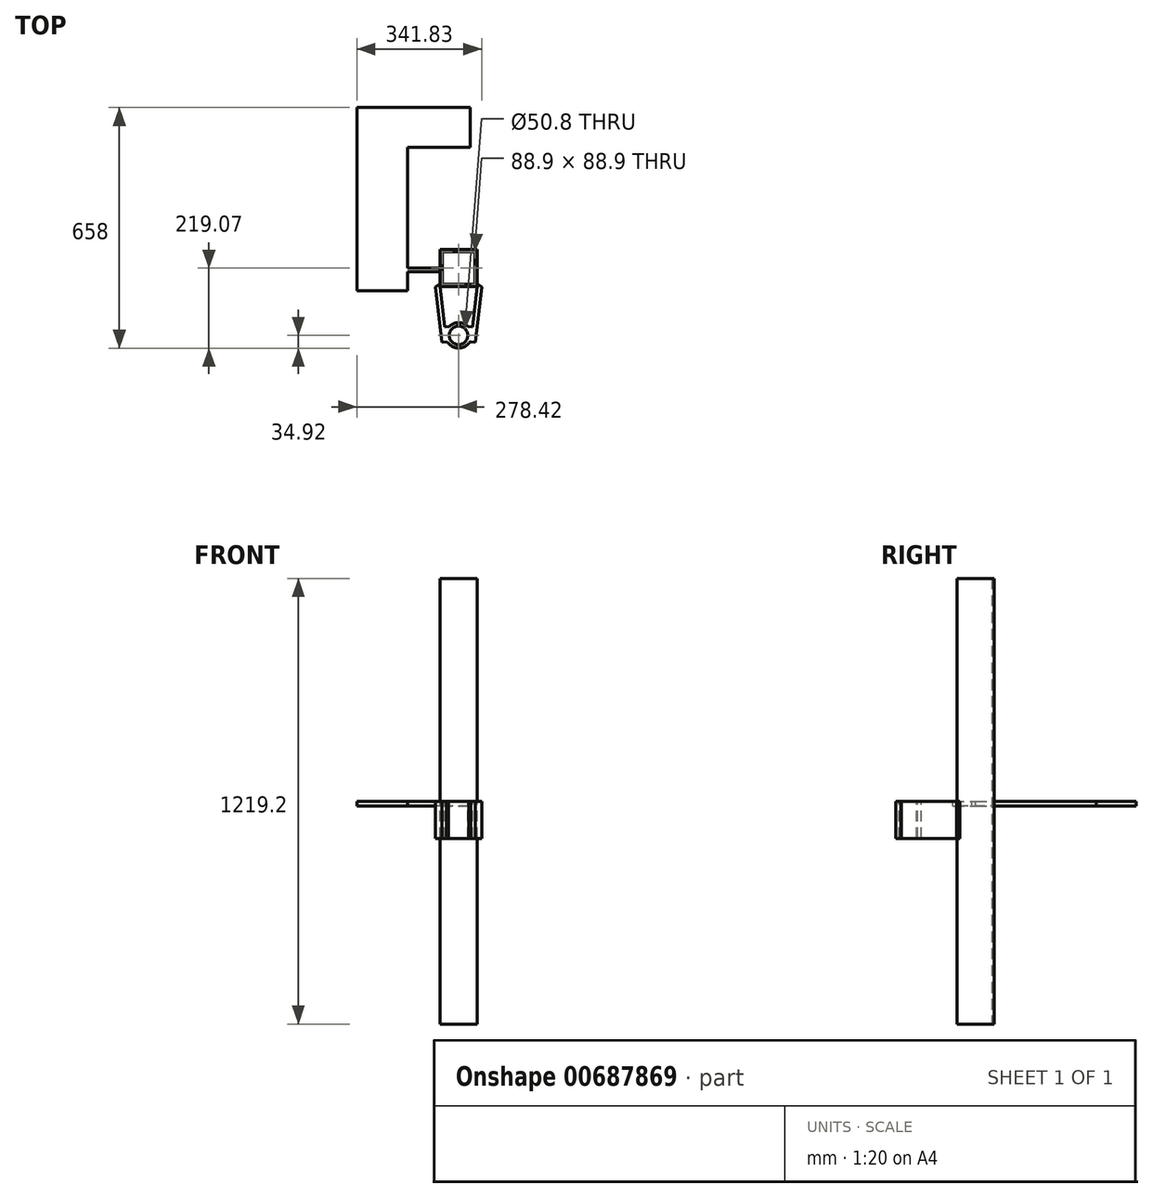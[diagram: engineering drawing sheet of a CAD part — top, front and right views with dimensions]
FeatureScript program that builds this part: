
annotation { "Feature Type Name" : "Feature", "Feature Type Description" : "" }
export const myFeature = defineFeature(function(context is Context, id is Id, definition is map)
    precondition{}
    {
        {
            var Q0;
            Q0=qCreatedBy(makeId("Top.planeOp"),FACE);
            var sketch = newSketch(context, id + "F0", { "sketchPlane" : qUnion([Q0])});
            skLineSegment(sketch, "E0.bottom", {"start": v(-50.8, -50.8) * mm, "end": v(50.8, -50.8) * mm});
            skLineSegment(sketch, "E0.top", {"start": v(-50.8, 50.8) * mm, "end": v(50.8, 50.8) * mm});
            skLineSegment(sketch, "E0.left", {"start": v(-50.8, -50.8) * mm, "end": v(-50.8, 50.8) * mm});
            skLineSegment(sketch, "E0.right", {"start": v(50.8, -50.8) * mm, "end": v(50.8, 50.8) * mm});
            skLineSegment(sketch, "E1.bottom", {"start": v(-44.45, 44.45) * mm, "end": v(44.45, 44.45) * mm});
            skLineSegment(sketch, "E1.top", {"start": v(-44.45, -44.45) * mm, "end": v(44.45, -44.45) * mm});
            skLineSegment(sketch, "E1.left", {"start": v(-44.45, 44.45) * mm, "end": v(-44.45, -44.45) * mm});
            skLineSegment(sketch, "E1.right", {"start": v(44.45, 44.45) * mm, "end": v(44.45, -44.45) * mm});
            skSolve(sketch);
        }
        {
            var Q0;
            Q0=makeQuery(id+"F0.imprint","IMPRINT",FACE,{"disambiguationData":[TD([[makeQuery(id+"F0.imprint","IMPRINT",EDGE,{"derivedFrom":sQuery(id+"F0.wireOp",EDGE,"E0.bottom")}),1.0]])]});
            extrude(context, id + "F1", {"entities" : qUnion([Q0]), "depth" : 1219.2 * mm, "offsetDistance" : 25.4 * mm});
        }
        {
            var Q0;
            Q0=qCreatedBy(makeId("Top.planeOp"),FACE);
            cPlane(context, id + "F2", {"entities" : qUnion([Q0]), "cplaneType" : CPlaneType.OFFSET, "offset" : 609.6 * mm, "width" : 152.4 * mm, "height" : 152.4 * mm});
        }
        {
            var Q0;
            Q0=qCreatedBy(id+"F2.planeOp",FACE);
            var sketch = newSketch(context, id + "F3", { "sketchPlane" : qUnion([Q0])});
            skLineSegment(sketch, "E2.0", {"start": v(-50.8, -50.8) * mm, "end": v(-50.8, 50.8) * mm});
            skLineSegment(sketch, "E3.0", {"start": v(-50.8, 50.8) * mm, "end": v(50.8, 50.8) * mm});
            skLineSegment(sketch, "E4.0", {"start": v(50.8, -50.8) * mm, "end": v(50.8, 50.8) * mm});
            skLineSegment(sketch, "E5.0", {"start": v(-50.8, -50.8) * mm, "end": v(50.8, -50.8) * mm});
            skCircle(sketch, "E6", {"center": v(0, -184.15) * mm, "radius": 34.93 * mm});
            skCircle(sketch, "E7", {"center": v(0, -184.15) * mm, "radius": 25.4 * mm});
            skLineSegment(sketch, "E8", {"start": v(-50.8, -50.8) * mm, "end": v(-33.05, -202.16) * mm});
            skLineSegment(sketch, "E9", {"start": v(50.8, -50.8) * mm, "end": v(33.05, -202.16) * mm});
            skLineSegment(sketch, "E10.0", {"start": v(-63.41, -52.28) * mm, "end": v(-45.67, -203.64) * mm});
            skLineSegment(sketch, "E11.0", {"start": v(63.41, -52.28) * mm, "end": v(45.67, -203.64) * mm});
            skLineSegment(sketch, "E12", {"start": v(-50.8, -50.8) * mm, "end": v(-63.41, -52.28) * mm});
            skLineSegment(sketch, "E13", {"start": v(63.41, -52.28) * mm, "end": v(50.8, -50.8) * mm});
            skLineSegment(sketch, "E14", {"start": v(45.67, -203.64) * mm, "end": v(33.05, -202.16) * mm});
            skLineSegment(sketch, "E15", {"start": v(-33.05, -202.16) * mm, "end": v(-45.67, -203.64) * mm});
            skLineSegment(sketch, "E16", {"start": v(-37.83, -161.4) * mm, "end": v(-25.16, -159.92) * mm});
            skLineSegment(sketch, "E17", {"start": v(37.83, -161.4) * mm, "end": v(25.16, -159.92) * mm});
            skLineSegment(sketch, "E18", {"start": v(33.05, -202.16) * mm, "end": v(28.17, -204.79) * mm});
            skLineSegment(sketch, "E19", {"start": v(-33.05, -202.16) * mm, "end": v(-27.98, -205.05) * mm});
            skLineSegment(sketch, "E20", {"start": v(-63.41, -52.28) * mm, "end": v(-50.8, -42.6) * mm});
            skLineSegment(sketch, "E21", {"start": v(63.41, -52.28) * mm, "end": v(50.8, -43.22) * mm});
            skSolve(sketch);
        }
        {
            var Q0;
            {var subQ0=sQuery(id+"F3.wireOp",EDGE,"E12");Q0=makeQuery(id+"F3.imprint","IMPRINT",FACE,{"disambiguationData":[TD([[makeQuery(id+"F3.imprint","IMPRINT",EDGE,{"derivedFrom":subQ0}),-1.0]])]});}
            var Q1;
            Q1=makeQuery(id+"F3.imprint","IMPRINT",FACE,{"disambiguationData":[TD([[makeQuery(id+"F3.imprint","IMPRINT",EDGE,{"derivedFrom":sQuery(id+"F3.wireOp",EDGE,"E10.0")}),1.0]])]});
            var Q2;
            Q2=makeQuery(id+"F3.imprint","IMPRINT",FACE,{"disambiguationData":[TD([[makeQuery(id+"F3.imprint","IMPRINT",EDGE,{"derivedFrom":sQuery(id+"F3.wireOp",EDGE,"E7")}),-1.0]])]});
            var Q3;
            {var subQ0=sQuery(id+"F3.wireOp",EDGE,"E16");Q3=makeQuery(id+"F3.imprint","IMPRINT",FACE,{"disambiguationData":[TD([[makeQuery(id+"F3.imprint","IMPRINT",EDGE,{"derivedFrom":subQ0}),-1.0]])]});}
            var Q4;
            {var subQ0=sQuery(id+"F3.wireOp",EDGE,"E19");Q4=makeQuery(id+"F3.imprint","IMPRINT",FACE,{"disambiguationData":[TD([[makeQuery(id+"F3.imprint","IMPRINT",EDGE,{"derivedFrom":subQ0}),1.0]])]});}
            var Q5;
            {var subQ0=sQuery(id+"F3.wireOp",EDGE,"E18");Q5=makeQuery(id+"F3.imprint","IMPRINT",FACE,{"disambiguationData":[TD([[makeQuery(id+"F3.imprint","IMPRINT",EDGE,{"derivedFrom":subQ0}),-1.0]])]});}
            var Q6;
            {var subQ0=sQuery(id+"F3.wireOp",EDGE,"E17");Q6=makeQuery(id+"F3.imprint","IMPRINT",FACE,{"disambiguationData":[TD([[makeQuery(id+"F3.imprint","IMPRINT",EDGE,{"derivedFrom":subQ0}),1.0]])]});}
            var Q7;
            Q7=makeQuery(id+"F3.imprint","IMPRINT",FACE,{"disambiguationData":[TD([[makeQuery(id+"F3.imprint","IMPRINT",EDGE,{"derivedFrom":sQuery(id+"F3.wireOp",EDGE,"E11.0")}),-1.0]])]});
            var Q8;
            {var subQ0=sQuery(id+"F3.wireOp",EDGE,"E13");Q8=makeQuery(id+"F3.imprint","IMPRINT",FACE,{"disambiguationData":[TD([[makeQuery(id+"F3.imprint","IMPRINT",EDGE,{"derivedFrom":subQ0}),-1.0]])]});}
            extrude(context, id + "F4", {"entities" : qUnion([Q0, Q1, Q2, Q3, Q4, Q5, Q6, Q7, Q8]), "operationType" : NewBodyOperationType.ADD, "oppositeDirection" : true, "depth" : 101.6 * mm, "offsetDistance" : 25.4 * mm});
        }
        {
            var Q0;
            Q0=qCreatedBy(id+"F2.planeOp",FACE);
            var sketch = newSketch(context, id + "F5", { "sketchPlane" : qUnion([Q0])});
            skLineSegment(sketch, "E22.0", {"start": v(-50.8, 50.8) * mm, "end": v(50.8, 50.8) * mm});
            skLineSegment(sketch, "E23.0", {"start": v(-50.8, -50.8) * mm, "end": v(-50.8, 50.8) * mm});
            skLineSegment(sketch, "E24.0", {"start": v(50.8, -50.8) * mm, "end": v(50.8, 50.8) * mm});
            skLineSegment(sketch, "E25", {"start": v(-139.7, -61.83) * mm, "end": v(-139.7, 330.2) * mm});
            skLineSegment(sketch, "E26", {"start": v(-139.7, 330.2) * mm, "end": v(31.27, 330.2) * mm});
            skLineSegment(sketch, "E27", {"start": v(31.27, 330.2) * mm, "end": v(31.27, 438.93) * mm});
            skLineSegment(sketch, "E28", {"start": v(31.27, 438.93) * mm, "end": v(-278.42, 438.93) * mm});
            skLineSegment(sketch, "E29", {"start": v(-278.42, 438.93) * mm, "end": v(-278.42, -61.83) * mm});
            skLineSegment(sketch, "E30", {"start": v(-278.42, -61.83) * mm, "end": v(-139.7, -61.83) * mm});
            skLineSegment(sketch, "E31", {"start": v(-50.8, -9.94) * mm, "end": v(-139.7, -9.94) * mm});
            skLineSegment(sketch, "E32", {"start": v(-139.7, -9.94) * mm, "end": v(-139.7, 0) * mm});
            skLineSegment(sketch, "E33", {"start": v(-139.7, 0) * mm, "end": v(-50.8, 0) * mm});
            skLineSegment(sketch, "E34.bottom", {"start": v(-33, 50.8) * mm, "end": v(-22.16, 50.8) * mm});
            skLineSegment(sketch, "E34.top", {"start": v(-33, 330.2) * mm, "end": v(-22.16, 330.2) * mm});
            skLineSegment(sketch, "E34.left", {"start": v(-33, 50.8) * mm, "end": v(-33, 330.2) * mm});
            skLineSegment(sketch, "E34.right", {"start": v(-22.16, 50.8) * mm, "end": v(-22.16, 330.2) * mm});
            skSolve(sketch);
        }
        {
            var Q0;
            Q0=makeQuery(id+"F5.imprint","IMPRINT",FACE,{"disambiguationData":[TD([[makeQuery(id+"F5.imprint","IMPRINT",EDGE,{"derivedFrom":sQuery(id+"F5.wireOp",EDGE,"E25")}),1.0]])]});
            var Q1;
            Q1=makeQuery(id+"F5.imprint","IMPRINT",FACE,{"disambiguationData":[TD([[makeQuery(id+"F5.imprint","IMPRINT",EDGE,{"derivedFrom":sQuery(id+"F5.wireOp",EDGE,"E34.bottom")}),1.0]])]});
            var Q2;
            {var subQ0=sQuery(id+"F5.wireOp",EDGE,"E31");Q2=makeQuery(id+"F5.imprint","IMPRINT",FACE,{"disambiguationData":[TD([[makeQuery(id+"F5.imprint","IMPRINT",EDGE,{"derivedFrom":subQ0}),-1.0]])]});}
            extrude(context, id + "F6", {"entities" : qUnion([Q0, Q1, Q2]), "oppositeDirection" : true, "depth" : 12.7 * mm, "offsetDistance" : 25.4 * mm});
        }
    });
